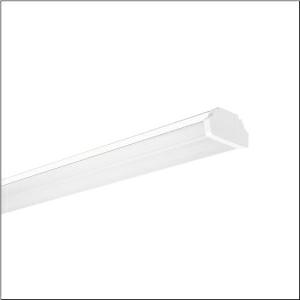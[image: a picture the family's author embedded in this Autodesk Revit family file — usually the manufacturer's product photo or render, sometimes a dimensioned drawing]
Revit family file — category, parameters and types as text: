
# Revit family: dus_r__31_mo_53bd812c1v6075_124e
name_source: partatom
category: Lighting Fixtures
units: mm (PartAtom-declared; Revit-internal decimal feet)

## family parameters
Cut with Voids When Loaded = No
Host = Face
Light Source = No
Part Type = Normal
Room Calculation Point = No
Round Connector Dimension = Use Diameter
Shared = No

## types (1)
- --- (1 x LED, 7640 lm, 48.9 W, 6500K)
    Apparent Load = 49 VA
    CIE Flux Codes = 47 80 95 92 100
    Color Rendering = 80
    Color Temperature = 6500K
    Default Elevation = 1800 mm
    Description = DUS® 31 MO, luminaire insert, of sheet steel, coil coated, white, length: 1.535mm, width: 81mm, height: 90mm, 5x system unit, system units: 307mm, LED rated luminous flux: 7.640lm, light colour: 865, control gear: ON/OFF Multilumen, CLOi, control gear: ECG Multilumen, with plug, 3-pole, with phase selection, mains connection: 220..240V, AC, 50/60Hz, start of lifetime: 49W, end of service life: 56W, through-wiring accessed according to module size, primary optical cover: cover, of PMMA, light emission: direct distribution, primary light characteristic: symmetric, protection rating (complete): IP20, protection rating (LED compartment): IP50, insulation class (complete): insulation class I (protective earthing), certification: CE, ENEC, VDE, UKCA, impact resistance: IK03, permissible ambient temperature for indoor applications: -35..+30°C, corresponds to IFS (International Featured Standards) requirements for safety and quality in the food industry, reducing of maximum allowable ambient temperature of 5°C with ceiling mounting, packaging unit: 1 piece
    Height = 95 mm
    Lamp = 1 x LED
    Lamp Light Flux = 7640 lm
    Lamp Power = 48.9 W
    Lamp count = 1
    Length = 1535 mm
    Luminous efficacy = 156 lm/W
    Manufacturer = Siteco
    ModVariant = No
    Model = 53BD812C1V6075
    Mounting Place = Ceiling
    Mounting Type = Pendant
    Number of Poles = 1
    OnlyDefault = Yes
    Power Factor = 1
    Product Name = DUS® 31 MO
    Product group = luminaire insert
    ProductGroupID = 901
    Protection Class = Protection class I
    Protection Degree = IP 20
    RLX_Detail_Level = 1
    RLX_Emergency_Light_Flux = 0 lm
    RLX_Emergency_Type = 0
    RLX_Emergency_Type_DB = No
    RlxData = <blob elided: 39837 chars, md5=8fe81e3a>
    Socket = socket
    Standby Power = 0 W
    System Light Flux = 7640 lm
    System Power = 49 W
    Type Comments = factory setting: luminous flux: 100 % | (A | C | E) | 107 mA
    Type Image = l_1003451.jpg
    URL = http://relux.com
    VarID = @adj_138143
    Voltage = 0 V
    Weight = 0.00 kg
    Width = 81 mm

## geometry (parser evidence)
native form markers: Blend x4, Sweep x12
no freeform markers — native parametric forms only
